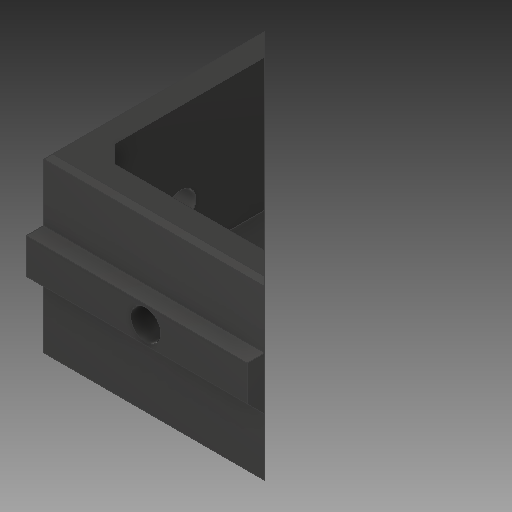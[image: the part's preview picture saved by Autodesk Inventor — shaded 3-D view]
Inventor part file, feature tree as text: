
AUTODESK INVENTOR PART (.ipt)
format: ipt  version: 2019 (Build 230136000, 136)  size: 169,984 bytes
history: native  units: mm
features: extrude x6, sketch x6, chamfer x4
ambient origin geometry x8: Origin, YZ Plane, XZ Plane, XY Plane, X Axis, Y Axis, Z Axis, Center Point
bodies: Solid1 (feature_tree)
feature tree (16):
  extrude  "Extrusion1"  Depth=20.0mm TaperAngle=0.0deg
  extrude  "Extrusion2"  Depth=3.0mm
  extrude  "Extrusion5"  Depth=4.0mm
  extrude  "Extrusion6"  Depth=1.0mm TaperAngle=0.0deg
  chamfer  "Chamfer4"  Distance=1.0mm Angle=45.0deg
  extrude  "Extrusion7"  Depth=1.0mm TaperAngle=0.0deg
  extrude  "Extrusion8"  Depth=1.0mm TaperAngle=0.0deg
  chamfer  "Chamfer5"  Distance=1.0mm Angle=45.0deg
  chamfer  "Chamfer6"  Distance=2.0mm Angle=45.0deg
  chamfer  "Chamfer7"  Distance=0.5mm Angle=45.0deg
  sketch  "Sketch1"  dims[d0=25.0mm d1=20.0mm d2=0.0mm]
  sketch  "Sketch2"  dims[d3=3.0mm d4=3.0mm]
  sketch  "Sketch5"  dims[d5=17.0mm d6=0.0mm d22=4.0mm]
  sketch  "Sketch6"  dims[d23=1.0mm d24=0.0mm d25=1.0mm d26=0.0mm d27=1.0mm d28=2.0mm d29=45.0deg]
  sketch  "Sketch7"  dims[d30=3.4mm d31=1.0mm d32=0.0mm]
  sketch  "Sketch8"  dims[d33=3.4mm d34=1.0mm d35=0.0mm d36=1.0mm d37=2.0mm d38=45.0deg d39=2.0mm d40=2.0mm d41=45.0deg d42=0.5mm d43=2.0mm d44=45.0deg]
